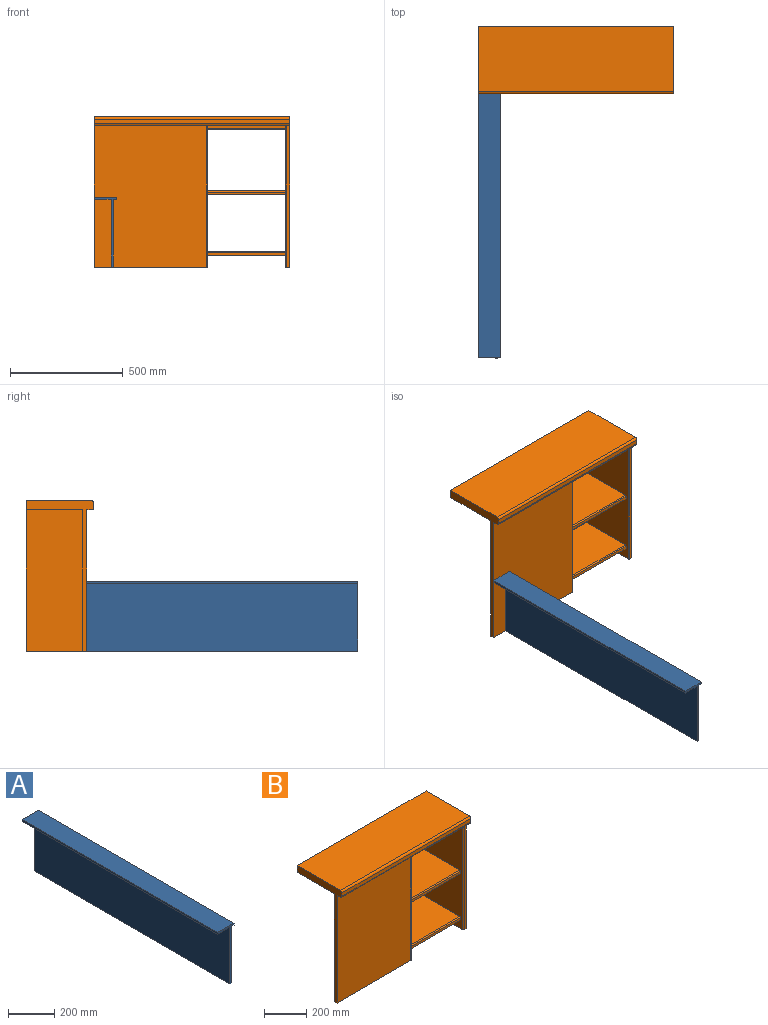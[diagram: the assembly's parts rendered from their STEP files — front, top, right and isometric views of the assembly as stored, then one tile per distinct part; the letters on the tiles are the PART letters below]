
ASSEMBLY  parts=2 mates=2
PART A: 10 faces, bbox 100x1200x310 mm
  f0: plane 310x100mm, normal (0,1,0), area 4000mm2, adj f2,f3,f4,f5,f6,f7,f8,f9
  f1: plane 310x100mm, normal (0,-1,0), area 4000mm2, adj f2,f3,f4,f5,f6,f7,f8,f9
  f2: plane 1200x10mm, normal (0,0,-1), area 12000mm2, adj f0,f1,f3,f4
  f3: plane 1200x300mm, normal (-1,0,0), area 360000mm2, adj f0,f1,f2,f5
  f4: plane 1200x300mm, normal (1,0,0), area 360000mm2, adj f0,f1,f2,f9
  f5: plane 1200x75mm, normal (0,0,-1), area 90000mm2, adj f0,f1,f3,f7
  f6: plane 1200x10mm, normal (1,0,0), area 12000mm2, adj f0,f1,f8,f9
  f7: plane 1200x10mm, normal (-1,0,0), area 12000mm2, adj f0,f1,f5,f8
  f8: plane 1200x100mm, normal (0,0,1), area 120000mm2, adj f0,f1,f6,f7
  f9: plane 1200x15mm, normal (0,0,-1), area 18000mm2, adj f0,f1,f4,f6
PART B: 36 faces, bbox 865x300x665 mm
  f0: plane 251.5x4mm, normal (0,1,0), area 1006mm2, adj f6,f7,f24,f34
  f1: plane 269.5x250mm, normal (1,0,0), area 67375mm2, adj f3,f14,f30,f33
  f2: plane 625x263mm, normal (-1,0,0), area 150891.1mm2, adj f4,f14,f20,f22,f23,f24,f25,f26
  f3: plane 269.5x4mm, normal (0,1,0), area 1078mm2, adj f1,f7,f30,f33
  f4: plane 865x40mm, normal (0,0,-1), area 25286.7mm2, adj f2,f7,f8,f11,f15,f18,f21,f22
  f5: plane 50x4mm, normal (0,1,0), area 200mm2, adj f7,f9,f12,f25
  f6: plane 251.5x250mm, normal (1,0,0), area 62875mm2, adj f0,f14,f24,f34
  f7: plane 625x18mm, normal (1,0,0), area 8141.1mm2, adj f0,f3,f4,f5,f9,f15,f23,f24
  f8: plane 665x300mm, normal (-1,0,0), area 23207.1mm2, adj f4,f9,f10,f11,f14,f16,f17,f19
  f9: plane 500x268mm, normal (0,0,-1), area 13494.6mm2, adj f5,f7,f8,f10,f11,f12,f13,f14
  f10: plane 625x478mm, normal (0,1,0), area 298750mm2, adj f8,f9,f13,f16
  f11: plane 625x495mm, normal (0,-1,0), area 309375mm2, adj f4,f8,f9,f15
  f12: plane 250x50mm, normal (1,0,0), area 12500mm2, adj f5,f9,f14,f25
  f13: plane 625x250mm, normal (-1,0,0), area 156250mm2, adj f9,f10,f14,f16
  f14: plane 865x665mm, normal (0,1,0), area 76054mm2, adj f1,f2,f6,f8,f9,f12,f13,f16
  f15: cylinder r=5mm len=625mm, axis (0,0,1), area 4908.7mm2, adj f4,f7,f9,f11
  f16: plane 478x250mm, normal (0,0,-1), area 119500mm2, adj f8,f10,f13,f14
  f17: plane 865x20mm, normal (0,-1,0), area 17300mm2, adj f8,f18,f27,f28
  f18: plane 665x300mm, normal (1,0,0), area 179457.1mm2, adj f4,f14,f17,f19,f20,f21,f27,f28
  f19: plane 865x290mm, normal (0,0,1), area 250850mm2, adj f8,f14,f18,f28
  f20: plane 268x18mm, normal (0,0,-1), area 4818.6mm2, adj f2,f14,f18,f21,f22
  f21: plane 625x13mm, normal (0,-1,0), area 8125mm2, adj f4,f18,f20,f22
  f22: cylinder r=5mm len=625mm, axis (0,0,-1), area 4908.7mm2, adj f2,f4,f20,f21
  f23: plane 347x13mm, normal (0,-1,0), area 4511mm2, adj f2,f7,f25,f26
  f24: plane 351x250mm, normal (0,0,1), area 86015mm2, adj f0,f2,f6,f7,f14,f26
  f25: plane 351x250mm, normal (0,0,-1), area 87750mm2, adj f2,f5,f12,f14,f23
  f26: cylinder r=5mm len=347mm, axis (-1,0,0), area 2725.3mm2, adj f2,f7,f23,f24
  f27: cylinder r=10mm len=865mm, axis (1,0,0), area 13587.4mm2, adj f4,f8,f17,f18
  f28: cylinder r=10mm len=865mm, axis (-1,0,0), area 13587.4mm2, adj f8,f17,f18,f19
  f29: plane 347x13mm, normal (0,-1,0), area 4511mm2, adj f2,f4,f7,f31
  f30: plane 351x250mm, normal (0,0,-1), area 86015mm2, adj f1,f2,f3,f7,f14,f31
  f31: cylinder r=5mm len=347mm, axis (1,0,0), area 2725.3mm2, adj f2,f7,f29,f30
  f32: plane 347x13mm, normal (0,-1,0), area 4511mm2, adj f2,f7,f34,f35
  f33: plane 351x250mm, normal (0,0,1), area 86015mm2, adj f1,f2,f3,f7,f14,f35
  f34: plane 351x250mm, normal (0,0,-1), area 87750mm2, adj f0,f2,f6,f14,f32
  f35: cylinder r=5mm len=347mm, axis (-1,0,0), area 2725.3mm2, adj f2,f7,f32,f33
PLACE A t=(42.4,122.5,231.52)mm
PLACE B t=(207.4,122.5,244.02)mm
MATE planar B.f8 <-> A.f7  axis (-1,0,0) through (-42.6,122.5,244.02)mm
MATE planar A.f2 <-> B.f9  axis (0,0,-1) through (37.4,122.5,-68.48)mm
